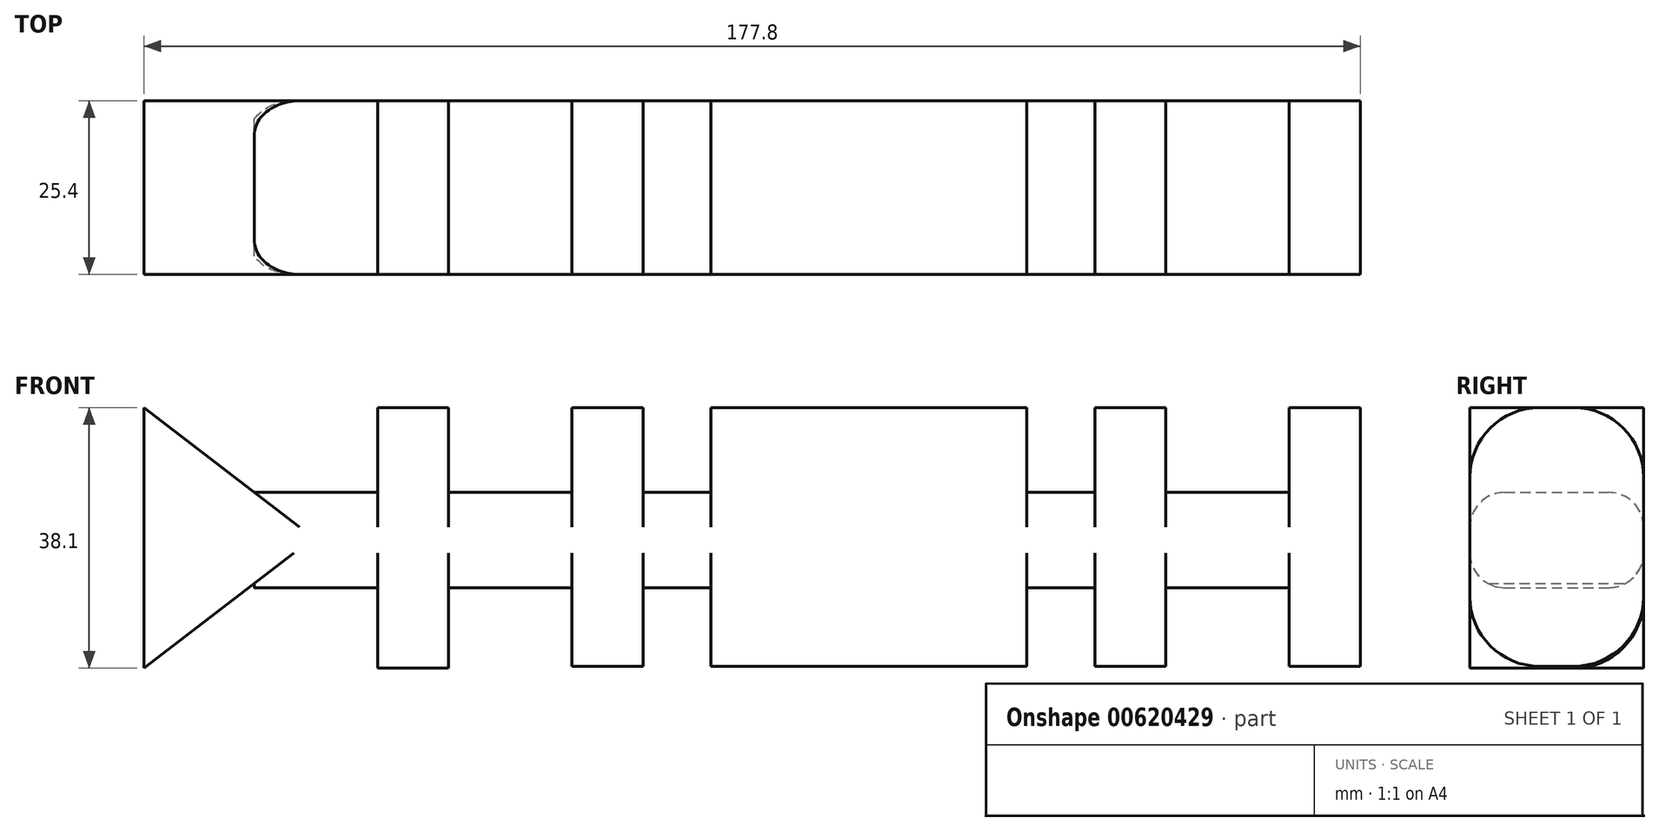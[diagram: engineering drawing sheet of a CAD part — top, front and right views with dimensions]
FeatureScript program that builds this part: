
annotation { "Feature Type Name" : "Feature", "Feature Type Description" : "" }
export const myFeature = defineFeature(function(context is Context, id is Id, definition is map)
    precondition{}
    {
        {
            var Q0;
            Q0=qCreatedBy(makeId("Front.planeOp"),FACE);
            var sketch = newSketch(context, id + "F0", { "sketchPlane" : qUnion([Q0])});
            skLineSegment(sketch, "E0", {"start": v(-76.86, 19.14) * mm, "end": v(-60.75, 6.75) * mm});
            skLineSegment(sketch, "E1", {"start": v(-60.75, -6.57) * mm, "end": v(-76.86, -18.96) * mm});
            skLineSegment(sketch, "E2", {"start": v(-76.86, -18.96) * mm, "end": v(-76.86, 19.14) * mm});
            skLineSegment(sketch, "E3", {"start": v(-60.75, 6.75) * mm, "end": v(-60.75, -6.57) * mm});
            skLineSegment(sketch, "E4.bottom", {"start": v(-60.75, 6.75) * mm, "end": v(-42.72, 6.75) * mm});
            skLineSegment(sketch, "E4.top", {"start": v(-60.75, -7.19) * mm, "end": v(-42.72, -7.19) * mm});
            skLineSegment(sketch, "E4.left", {"start": v(-60.75, 6.75) * mm, "end": v(-60.75, -7.19) * mm});
            skLineSegment(sketch, "E4.right", {"start": v(-42.72, 6.75) * mm, "end": v(-42.72, -7.19) * mm});
            skLineSegment(sketch, "E5.bottom", {"start": v(-42.72, 19.14) * mm, "end": v(-32.32, 19.14) * mm});
            skLineSegment(sketch, "E5.top", {"start": v(-42.72, -18.96) * mm, "end": v(-32.32, -18.96) * mm});
            skLineSegment(sketch, "E5.left", {"start": v(-42.72, 19.14) * mm, "end": v(-42.72, -18.96) * mm});
            skLineSegment(sketch, "E5.right", {"start": v(-32.32, 19.14) * mm, "end": v(-32.32, -18.96) * mm});
            skLineSegment(sketch, "E6.bottom", {"start": v(-32.32, 6.75) * mm, "end": v(-14.29, 6.75) * mm});
            skLineSegment(sketch, "E6.top", {"start": v(-32.32, -7.19) * mm, "end": v(-14.29, -7.19) * mm});
            skLineSegment(sketch, "E6.left", {"start": v(-32.32, 6.75) * mm, "end": v(-32.32, -7.19) * mm});
            skLineSegment(sketch, "E6.right", {"start": v(-14.29, 6.75) * mm, "end": v(-14.29, -7.19) * mm});
            skLineSegment(sketch, "E7.bottom", {"start": v(-14.29, 19.14) * mm, "end": v(-3.9, 19.14) * mm});
            skLineSegment(sketch, "E7.top", {"start": v(-14.29, -18.68) * mm, "end": v(-3.9, -18.68) * mm});
            skLineSegment(sketch, "E7.left", {"start": v(-14.29, 19.14) * mm, "end": v(-14.29, -18.68) * mm});
            skLineSegment(sketch, "E7.right", {"start": v(-3.9, 19.14) * mm, "end": v(-3.9, -18.68) * mm});
            skLineSegment(sketch, "E8.bottom", {"start": v(-3.9, 6.75) * mm, "end": v(6.03, 6.75) * mm});
            skLineSegment(sketch, "E8.top", {"start": v(-3.9, -7.19) * mm, "end": v(6.03, -7.19) * mm});
            skLineSegment(sketch, "E8.left", {"start": v(-3.9, 6.75) * mm, "end": v(-3.9, -7.19) * mm});
            skLineSegment(sketch, "E8.right", {"start": v(6.03, 6.75) * mm, "end": v(6.03, -7.19) * mm});
            skLineSegment(sketch, "E9.bottom", {"start": v(6.03, 19.14) * mm, "end": v(52.2, 19.14) * mm});
            skLineSegment(sketch, "E9.top", {"start": v(6.03, -18.68) * mm, "end": v(52.2, -18.68) * mm});
            skLineSegment(sketch, "E9.left", {"start": v(6.03, 19.14) * mm, "end": v(6.03, -18.68) * mm});
            skLineSegment(sketch, "E9.right", {"start": v(52.2, 19.14) * mm, "end": v(52.2, -18.68) * mm});
            skLineSegment(sketch, "E10.bottom", {"start": v(52.2, 6.75) * mm, "end": v(62.12, 6.75) * mm});
            skLineSegment(sketch, "E10.top", {"start": v(52.2, -7.19) * mm, "end": v(62.12, -7.19) * mm});
            skLineSegment(sketch, "E10.left", {"start": v(52.2, 6.75) * mm, "end": v(52.2, -7.19) * mm});
            skLineSegment(sketch, "E10.right", {"start": v(62.12, 6.75) * mm, "end": v(62.12, -7.19) * mm});
            skLineSegment(sketch, "E11.bottom", {"start": v(62.12, 19.14) * mm, "end": v(72.51, 19.14) * mm});
            skLineSegment(sketch, "E11.top", {"start": v(62.12, -18.68) * mm, "end": v(72.51, -18.68) * mm});
            skLineSegment(sketch, "E11.left", {"start": v(62.12, 19.14) * mm, "end": v(62.12, -18.68) * mm});
            skLineSegment(sketch, "E11.right", {"start": v(72.51, 19.14) * mm, "end": v(72.51, -18.68) * mm});
            skLineSegment(sketch, "E12.bottom", {"start": v(72.51, 6.75) * mm, "end": v(90.55, 6.75) * mm});
            skLineSegment(sketch, "E12.top", {"start": v(72.51, -7.19) * mm, "end": v(90.55, -7.19) * mm});
            skLineSegment(sketch, "E12.left", {"start": v(72.51, 6.75) * mm, "end": v(72.51, -7.19) * mm});
            skLineSegment(sketch, "E12.right", {"start": v(90.55, 6.75) * mm, "end": v(90.55, -7.19) * mm});
            skLineSegment(sketch, "E13.bottom", {"start": v(90.55, 19.14) * mm, "end": v(100.94, 19.14) * mm});
            skLineSegment(sketch, "E13.top", {"start": v(90.55, -18.68) * mm, "end": v(100.94, -18.68) * mm});
            skLineSegment(sketch, "E13.left", {"start": v(90.55, 19.14) * mm, "end": v(90.55, -18.68) * mm});
            skLineSegment(sketch, "E13.right", {"start": v(100.94, 19.14) * mm, "end": v(100.94, -18.68) * mm});
            skSolve(sketch);
        }
        {
            var Q0;
            Q0 = qSketchRegion(id + "F0", true);
            extrude(context, id + "F1", {"entities" : qUnion([Q0]), "depth" : 25.4 * mm, "offsetDistance" : 25.4 * mm});
        }
        {
            var Q0;
            Q0=makeQuery(id+"F1.opExtrude","CAP_EDGE",EDGE,{"disambiguationData":[OSD([sQuery(id+"F0.wireOp",EDGE,"E11.top")])],"isStart":true});
            var Q1;
            Q1=makeQuery(id+"F1.opExtrude","CAP_EDGE",EDGE,{"disambiguationData":[OSD([sQuery(id+"F0.wireOp",EDGE,"E11.top")])],"isStart":false});
            var Q2;
            Q2=makeQuery(id+"F1.opExtrude","CAP_EDGE",EDGE,{"disambiguationData":[OSD([sQuery(id+"F0.wireOp",EDGE,"E13.top")])],"isStart":true});
            var Q3;
            Q3=makeQuery(id+"F1.opExtrude","CAP_EDGE",EDGE,{"disambiguationData":[OSD([sQuery(id+"F0.wireOp",EDGE,"E13.top")])],"isStart":false});
            var Q4;
            Q4=makeQuery(id+"F1.opExtrude","CAP_EDGE",EDGE,{"disambiguationData":[OSD([sQuery(id+"F0.wireOp",EDGE,"E13.bottom")])],"isStart":false});
            var Q5;
            Q5=makeQuery(id+"F1.opExtrude","CAP_EDGE",EDGE,{"disambiguationData":[OSD([sQuery(id+"F0.wireOp",EDGE,"E13.bottom")])],"isStart":true});
            var Q6;
            Q6=makeQuery(id+"F1.opExtrude","CAP_EDGE",EDGE,{"disambiguationData":[OSD([sQuery(id+"F0.wireOp",EDGE,"E11.bottom")])],"isStart":false});
            var Q7;
            Q7=makeQuery(id+"F1.opExtrude","CAP_EDGE",EDGE,{"disambiguationData":[OSD([sQuery(id+"F0.wireOp",EDGE,"E11.bottom")])],"isStart":true});
            var Q8;
            Q8=makeQuery(id+"F1.opExtrude","CAP_EDGE",EDGE,{"disambiguationData":[OSD([sQuery(id+"F0.wireOp",EDGE,"E9.bottom")])],"isStart":false});
            var Q9;
            Q9=makeQuery(id+"F1.opExtrude","CAP_EDGE",EDGE,{"disambiguationData":[OSD([sQuery(id+"F0.wireOp",EDGE,"E9.bottom")])],"isStart":true});
            var Q10;
            Q10=makeQuery(id+"F1.opExtrude","CAP_EDGE",EDGE,{"disambiguationData":[OSD([sQuery(id+"F0.wireOp",EDGE,"E9.top")])],"isStart":false});
            var Q11;
            Q11=makeQuery(id+"F1.opExtrude","CAP_EDGE",EDGE,{"disambiguationData":[OSD([sQuery(id+"F0.wireOp",EDGE,"E9.top")])],"isStart":true});
            var Q12;
            Q12=makeQuery(id+"F1.opExtrude","CAP_EDGE",EDGE,{"disambiguationData":[OSD([sQuery(id+"F0.wireOp",EDGE,"E7.bottom")])],"isStart":true});
            var Q13;
            Q13=makeQuery(id+"F1.opExtrude","CAP_EDGE",EDGE,{"disambiguationData":[OSD([sQuery(id+"F0.wireOp",EDGE,"E7.top")])],"isStart":true});
            var Q14;
            Q14=makeQuery(id+"F1.opExtrude","CAP_EDGE",EDGE,{"disambiguationData":[OSD([sQuery(id+"F0.wireOp",EDGE,"E7.bottom")])],"isStart":false});
            var Q15;
            Q15=makeQuery(id+"F1.opExtrude","CAP_EDGE",EDGE,{"disambiguationData":[OSD([sQuery(id+"F0.wireOp",EDGE,"E7.top")])],"isStart":false});
            var Q16;
            Q16=makeQuery(id+"F1.opExtrude","CAP_EDGE",EDGE,{"disambiguationData":[OSD([sQuery(id+"F0.wireOp",EDGE,"E5.bottom")])],"isStart":true});
            var Q17;
            Q17=makeQuery(id+"F1.opExtrude","CAP_EDGE",EDGE,{"disambiguationData":[OSD([sQuery(id+"F0.wireOp",EDGE,"E5.top")])],"isStart":true});
            var Q18;
            Q18=makeQuery(id+"F1.opExtrude","CAP_EDGE",EDGE,{"disambiguationData":[OSD([sQuery(id+"F0.wireOp",EDGE,"E5.bottom")])],"isStart":false});
            fillet(context, id + "F2", {"entities" : qUnion([Q0, Q1, Q2, Q3, Q4, Q5, Q6, Q7, Q8, Q9, Q10, Q11, Q12, Q13, Q14, Q15, Q16, Q17, Q18]), "radius" : 10.16 * mm, "tangentPropagation" : true, "allowEdgeOverflow" : false});
        }
        {
            var Q0;
            Q0=makeQuery(id+"F1.opExtrude","CAP_EDGE",EDGE,{"disambiguationData":[OSD([sQuery(id+"F0.wireOp",EDGE,"E4.bottom")])],"isStart":false});
            var Q1;
            Q1=makeQuery(id+"F1.opExtrude","CAP_EDGE",EDGE,{"disambiguationData":[OSD([sQuery(id+"F0.wireOp",EDGE,"E4.top")])],"isStart":false});
            var Q2;
            Q2=makeQuery(id+"F1.opExtrude","CAP_EDGE",EDGE,{"disambiguationData":[OSD([sQuery(id+"F0.wireOp",EDGE,"E4.bottom")])],"isStart":true});
            var Q3;
            Q3=makeQuery(id+"F1.opExtrude","CAP_EDGE",EDGE,{"disambiguationData":[OSD([sQuery(id+"F0.wireOp",EDGE,"E4.top")])],"isStart":true});
            var Q4;
            Q4=makeQuery(id+"F1.opExtrude","CAP_EDGE",EDGE,{"disambiguationData":[OSD([sQuery(id+"F0.wireOp",EDGE,"E6.bottom")])],"isStart":true});
            var Q5;
            Q5=makeQuery(id+"F1.opExtrude","CAP_EDGE",EDGE,{"disambiguationData":[OSD([sQuery(id+"F0.wireOp",EDGE,"E6.top")])],"isStart":true});
            var Q6;
            Q6=makeQuery(id+"F1.opExtrude","CAP_EDGE",EDGE,{"disambiguationData":[OSD([sQuery(id+"F0.wireOp",EDGE,"E6.bottom")])],"isStart":false});
            var Q7;
            Q7=makeQuery(id+"F1.opExtrude","CAP_EDGE",EDGE,{"disambiguationData":[OSD([sQuery(id+"F0.wireOp",EDGE,"E6.top")])],"isStart":false});
            var Q8;
            Q8=makeQuery(id+"F1.opExtrude","CAP_EDGE",EDGE,{"disambiguationData":[OSD([sQuery(id+"F0.wireOp",EDGE,"E8.bottom")])],"isStart":false});
            var Q9;
            Q9=makeQuery(id+"F1.opExtrude","CAP_EDGE",EDGE,{"disambiguationData":[OSD([sQuery(id+"F0.wireOp",EDGE,"E8.top")])],"isStart":false});
            var Q10;
            Q10=makeQuery(id+"F1.opExtrude","CAP_EDGE",EDGE,{"disambiguationData":[OSD([sQuery(id+"F0.wireOp",EDGE,"E8.bottom")])],"isStart":true});
            var Q11;
            Q11=makeQuery(id+"F1.opExtrude","CAP_EDGE",EDGE,{"disambiguationData":[OSD([sQuery(id+"F0.wireOp",EDGE,"E8.top")])],"isStart":true});
            var Q12;
            Q12=makeQuery(id+"F1.opExtrude","CAP_EDGE",EDGE,{"disambiguationData":[OSD([sQuery(id+"F0.wireOp",EDGE,"E12.bottom")])],"isStart":true});
            var Q13;
            Q13=makeQuery(id+"F1.opExtrude","CAP_EDGE",EDGE,{"disambiguationData":[OSD([sQuery(id+"F0.wireOp",EDGE,"E12.bottom")])],"isStart":false});
            var Q14;
            Q14=makeQuery(id+"F1.opExtrude","CAP_EDGE",EDGE,{"disambiguationData":[OSD([sQuery(id+"F0.wireOp",EDGE,"E12.top")])],"isStart":false});
            var Q15;
            Q15=makeQuery(id+"F1.opExtrude","CAP_EDGE",EDGE,{"disambiguationData":[OSD([sQuery(id+"F0.wireOp",EDGE,"E12.top")])],"isStart":true});
            var Q16;
            Q16=makeQuery(id+"F1.opExtrude","CAP_EDGE",EDGE,{"disambiguationData":[OSD([sQuery(id+"F0.wireOp",EDGE,"E10.bottom")])],"isStart":true});
            var Q17;
            Q17=makeQuery(id+"F1.opExtrude","CAP_EDGE",EDGE,{"disambiguationData":[OSD([sQuery(id+"F0.wireOp",EDGE,"E10.bottom")])],"isStart":false});
            var Q18;
            Q18=makeQuery(id+"F1.opExtrude","CAP_EDGE",EDGE,{"disambiguationData":[OSD([sQuery(id+"F0.wireOp",EDGE,"E10.top")])],"isStart":true});
            var Q19;
            Q19=makeQuery(id+"F1.opExtrude","CAP_EDGE",EDGE,{"disambiguationData":[OSD([sQuery(id+"F0.wireOp",EDGE,"E10.top")])],"isStart":false});
            fillet(context, id + "F3", {"entities" : qUnion([Q0, Q1, Q2, Q3, Q4, Q5, Q6, Q7, Q8, Q9, Q10, Q11, Q12, Q13, Q14, Q15, Q16, Q17, Q18, Q19]), "radius" : 5.08 * mm, "tangentPropagation" : true, "allowEdgeOverflow" : false});
        }
    });
